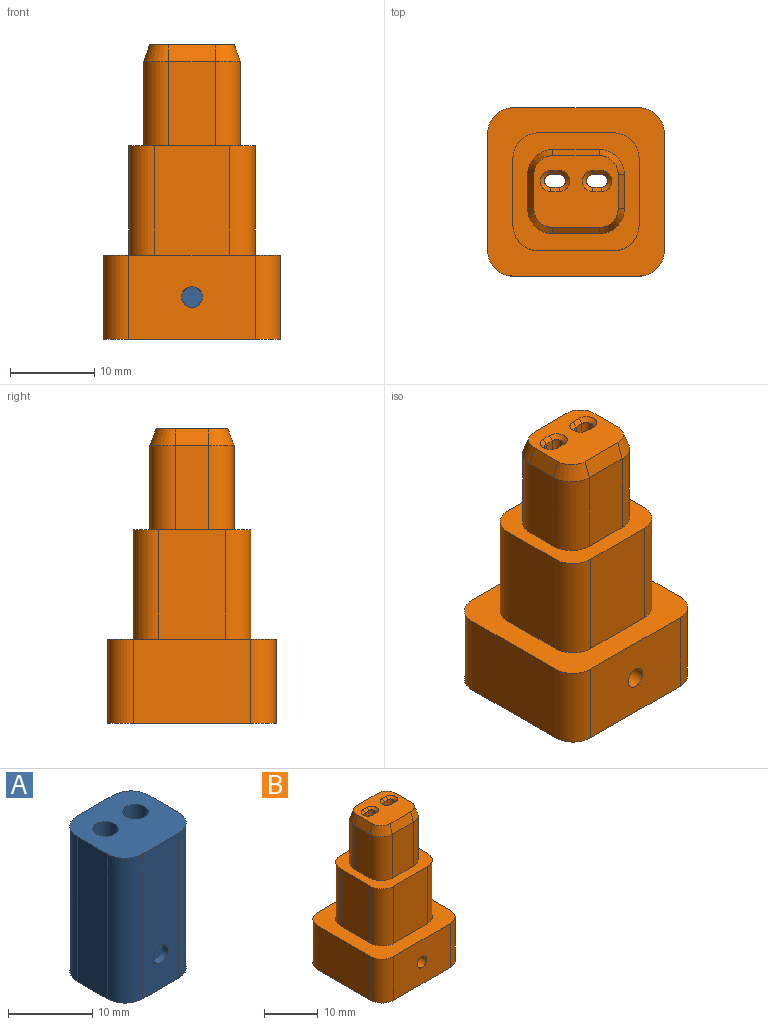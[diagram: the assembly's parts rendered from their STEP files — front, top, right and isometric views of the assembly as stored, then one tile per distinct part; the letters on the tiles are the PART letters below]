
ASSEMBLY  parts=2 mates=1
PART A: 14 faces, bbox 12x11x21 mm
  f0: plane 21x5mm, normal (1,0,0), area 105mm2, adj f1,f7,f8,f10
  f1: cylinder r=3mm len=21mm, axis (0,0,1), area 99mm2, adj f0,f2,f8,f10
  f2: plane 21x6mm, normal (0,-1,0), area 121.1mm2, adj f1,f3,f8,f10,f12
  f3: cylinder r=3mm len=21mm, axis (0,0,1), area 99mm2, adj f2,f4,f8,f10
  f4: plane 21x5mm, normal (-1,0,0), area 105mm2, adj f3,f8,f9,f10
  f5: cylinder r=1.5mm len=21mm, axis (0,0,1), area 197.9mm2, adj f8,f10
  f6: cylinder r=1.5mm len=21mm, axis (0,0,1), area 197.9mm2, adj f8,f10
  f7: cylinder r=3mm len=21mm, axis (0,0,1), area 99mm2, adj f0,f8,f10,f11
  f8: plane 12x11mm, normal (0,0,1), area 110.1mm2, adj f0,f1,f2,f3,f4,f5,f6,f7
  f9: cylinder r=3mm len=21mm, axis (0,0,1), area 99mm2, adj f4,f8,f10,f11
  f10: plane 12x11mm, normal (0,0,-1), area 110.1mm2, adj f0,f1,f2,f3,f4,f5,f6,f7
  f11: plane 21x6mm, normal (0,1,0), area 126mm2, adj f7,f8,f9,f10
  f12: cylinder r=1.25mm len=2.5mm, axis (0,-1,0), area 7.9mm2, adj f2,f13
  f13: plane 2.5x2.5mm, normal (0,-1,0), area 4.9mm2, adj f12
PART B: 66 faces, bbox 21x20x35 mm
  f0: plane 21x20mm, normal (0,0,-1), area 270.5mm2, adj f2,f3,f4,f5,f6,f7,f8,f9
  f1: cylinder r=1.25mm len=4.25mm, axis (0,-1,0), area 33.4mm2, adj f2,f58
  f2: plane 15x10mm, normal (0,-1,0), area 145.1mm2, adj f0,f1,f3,f9,f10
  f3: cylinder r=3mm len=10mm, axis (0,0,-1), area 47.1mm2, adj f0,f2,f4,f10
  f4: plane 14x10mm, normal (-1,0,0), area 140mm2, adj f0,f3,f5,f10
  f5: cylinder r=3mm len=10mm, axis (0,0,-1), area 47.1mm2, adj f0,f4,f6,f10
  f6: plane 15x10mm, normal (0,1,0), area 150mm2, adj f0,f5,f7,f10
  f7: cylinder r=3mm len=10mm, axis (0,0,-1), area 47.1mm2, adj f0,f6,f8,f10
  f8: plane 14x10mm, normal (1,0,0), area 140mm2, adj f0,f7,f9,f10
  f9: cylinder r=3mm len=10mm, axis (0,0,-1), area 47.1mm2, adj f0,f2,f8,f10
  f10: plane 21x20mm, normal (0,0,1), area 210mm2, adj f2,f3,f4,f5,f6,f7,f8,f9
  f11: plane 12.5x11.5mm, normal (0,0,-1), area 124.7mm2, adj f20,f21,f58,f59,f60,f61,f62,f63
  f12: plane 13x9mm, normal (0,-1,0), area 117mm2, adj f10,f13,f19,f22
  f13: cylinder r=3mm len=13mm, axis (0,0,-1), area 61.3mm2, adj f10,f12,f14,f22
  f14: plane 13x8mm, normal (-1,0,0), area 104mm2, adj f10,f13,f15,f22
  f15: cylinder r=3mm len=13mm, axis (0,0,-1), area 61.3mm2, adj f10,f14,f16,f22
  f16: plane 13x9mm, normal (0,1,0), area 117mm2, adj f10,f15,f17,f22
  f17: cylinder r=3mm len=13mm, axis (0,0,-1), area 61.3mm2, adj f10,f16,f18,f22
  f18: plane 13x8mm, normal (1,0,0), area 104mm2, adj f10,f17,f19,f22
  f19: cylinder r=3mm len=13mm, axis (0,0,-1), area 61.3mm2, adj f10,f12,f18,f22
  f20: cylinder r=1.65mm len=11.5mm, axis (0,0,1), area 119.2mm2, adj f11,f23
  f21: cylinder r=1.65mm len=11.5mm, axis (0,0,1), area 119.2mm2, adj f11,f24
  f22: plane 15x14mm, normal (0,0,1), area 95mm2, adj f12,f13,f14,f15,f16,f17,f18,f19
  f23: plane 3.3x3.3mm, normal (0,0,-1), area 5.3mm2, adj f20,f33,f34,f35,f36
  f24: plane 3.3x3.3mm, normal (0,0,-1), area 5.3mm2, adj f21,f37,f38,f39,f40
  f25: plane 10x5.5mm, normal (0,-1,0), area 55mm2, adj f22,f26,f32,f41
  f26: cylinder r=3mm len=10mm, axis (0,0,-1), area 47.1mm2, adj f22,f25,f27,f42
  f27: plane 10x4mm, normal (1,0,0), area 40mm2, adj f22,f26,f28,f43
  f28: cylinder r=3mm len=10mm, axis (0,0,-1), area 47.1mm2, adj f22,f27,f29,f44
  f29: plane 10x5.5mm, normal (0,1,0), area 55mm2, adj f22,f28,f30,f45
  f30: cylinder r=3mm len=10mm, axis (0,0,-1), area 47.1mm2, adj f22,f29,f31,f46
  f31: plane 10x4mm, normal (-1,0,0), area 40mm2, adj f22,f30,f32,f47
  f32: cylinder r=3mm len=10mm, axis (0,0,-1), area 47.1mm2, adj f22,f25,f31,f48
  f33: cylinder r=0.75mm len=2mm, axis (0,0,-1), area 4.7mm2, adj f23,f34,f36,f49
  f34: plane 2x1mm, normal (0,-1,0), area 2mm2, adj f23,f33,f35,f50
  f35: cylinder r=0.75mm len=2mm, axis (0,0,-1), area 4.7mm2, adj f23,f34,f36,f51
  f36: plane 2x1mm, normal (0,1,0), area 2mm2, adj f23,f33,f35,f52
  f37: plane 2x1mm, normal (0,-1,0), area 2mm2, adj f24,f38,f40,f53
  f38: cylinder r=0.75mm len=2mm, axis (0,0,-1), area 4.7mm2, adj f24,f37,f39,f54
  f39: plane 2x1mm, normal (0,1,0), area 2mm2, adj f24,f38,f40,f55
  f40: cylinder r=0.75mm len=2mm, axis (0,0,-1), area 4.7mm2, adj f24,f37,f39,f56
  f41: plane 5.5x2mm, normal (0,-0.94,0.34), area 11.7mm2, adj f25,f42,f48,f57
  f42: cone r=2.62mm half-angle=20deg, axis (0,0,-1), area 8.8mm2, adj f26,f41,f43,f57
  f43: plane 4x2mm, normal (0.94,0,0.34), area 8.5mm2, adj f27,f42,f44,f57
  f44: cone r=2.62mm half-angle=20deg, axis (0,0,-1), area 8.8mm2, adj f28,f43,f45,f57
  f45: plane 5.5x2mm, normal (0,0.94,0.34), area 11.7mm2, adj f29,f44,f46,f57
  f46: cone r=2.62mm half-angle=20deg, axis (0,0,-1), area 8.8mm2, adj f30,f45,f47,f57
  f47: plane 4x2mm, normal (-0.94,0,0.34), area 8.5mm2, adj f31,f46,f48,f57
  f48: cone r=2.62mm half-angle=20deg, axis (0,0,-1), area 8.8mm2, adj f32,f41,f47,f57
  f49: cone r=0mm half-angle=45deg, axis (0,0,1), area 2.2mm2, adj f33,f50,f52,f57
  f50: plane 1x0.5mm, normal (0,-0.71,0.71), area 0.7mm2, adj f34,f49,f51,f57
  f51: cone r=0mm half-angle=45deg, axis (0,0,1), area 2.2mm2, adj f35,f50,f52,f57
  f52: plane 1x0.5mm, normal (0,0.71,0.71), area 0.7mm2, adj f36,f49,f51,f57
  f53: plane 1x0.5mm, normal (0,-0.71,0.71), area 0.7mm2, adj f37,f54,f56,f57
  f54: cone r=0mm half-angle=45deg, axis (0,0,1), area 2.2mm2, adj f38,f53,f55,f57
  f55: plane 1x0.5mm, normal (0,0.71,0.71), area 0.7mm2, adj f39,f54,f56,f57
  f56: cone r=0mm half-angle=45deg, axis (0,0,1), area 2.2mm2, adj f40,f53,f55,f57
  f57: plane 10.04x8.54mm, normal (0,0,1), area 66.6mm2, adj f41,f42,f43,f44,f45,f46,f47,f48
  f58: plane 21x9.5mm, normal (0,1,0), area 194.6mm2, adj f0,f1,f11,f60,f61
  f59: plane 21x8.5mm, normal (-1,0,0), area 178.5mm2, adj f0,f11,f60,f65
  f60: cylinder r=1.5mm len=21mm, axis (0,0,-1), area 49.5mm2, adj f0,f11,f58,f59
  f61: cylinder r=1.5mm len=21mm, axis (0,0,-1), area 49.5mm2, adj f0,f11,f58,f62
  f62: plane 21x8.5mm, normal (1,0,0), area 178.5mm2, adj f0,f11,f61,f63
  f63: cylinder r=1.5mm len=21mm, axis (0,0,-1), area 49.5mm2, adj f0,f11,f62,f64
  f64: plane 21x9.5mm, normal (0,-1,0), area 199.5mm2, adj f0,f11,f63,f65
  f65: cylinder r=1.5mm len=21mm, axis (0,0,-1), area 49.5mm2, adj f0,f11,f59,f64
PLACE A t=(-15.97,3.99,-0.63)mm
PLACE B t=(-15.97,3.99,-0.63)mm fixed
MATE planar A.f1 <-> B.f11  axis (0,0,1) through (-12.97,1.49,20.37)mm
